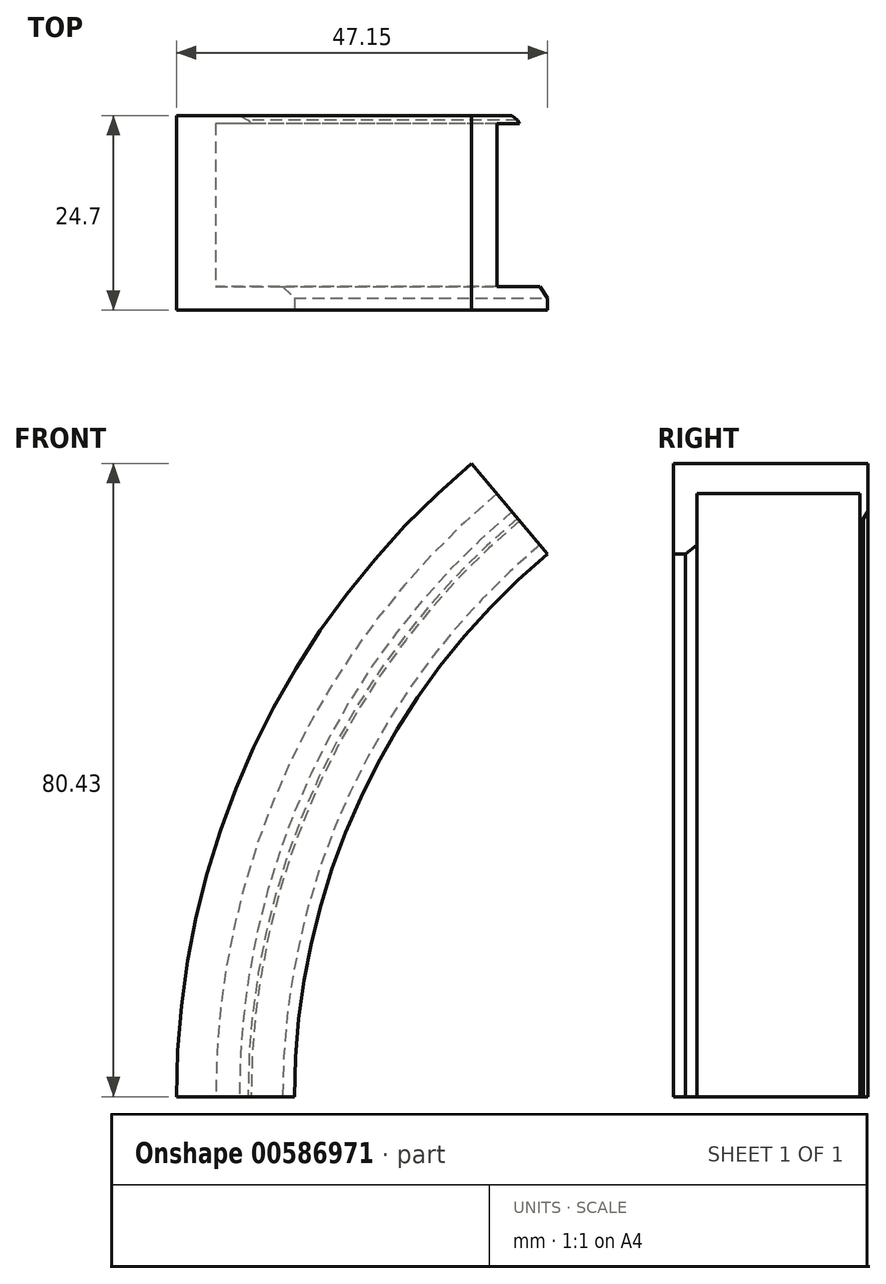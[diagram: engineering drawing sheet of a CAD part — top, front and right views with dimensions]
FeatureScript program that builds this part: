
annotation { "Feature Type Name" : "Feature", "Feature Type Description" : "" }
export const myFeature = defineFeature(function(context is Context, id is Id, definition is map)
    precondition{}
    {
        {
            var Q0;
            Q0=qCreatedBy(makeId("Top.planeOp"),FACE);
            var sketch = newSketch(context, id + "F0", { "sketchPlane" : qUnion([Q0])});
            skLineSegment(sketch, "E0", {"start": v(-100, -10) * mm, "end": v(-90, -10) * mm});
            skLineSegment(sketch, "E1", {"start": v(-90, -10) * mm, "end": v(-90, -13) * mm});
            skLineSegment(sketch, "E2", {"start": v(-90, -13) * mm, "end": v(-105, -13) * mm});
            skLineSegment(sketch, "E3", {"start": v(-105, -13) * mm, "end": v(-105, 11.7) * mm});
            skLineSegment(sketch, "E4", {"start": v(-105, 11.7) * mm, "end": v(-97, 11.7) * mm});
            skLineSegment(sketch, "E5", {"start": v(-97, 11.7) * mm, "end": v(-95, 10.7) * mm});
            skLineSegment(sketch, "E6", {"start": v(-95, 10.7) * mm, "end": v(-100, 10.7) * mm});
            skLineSegment(sketch, "E7", {"start": v(-100, 10.7) * mm, "end": v(-100, -10) * mm});
            skLineSegment(sketch, "E8", {"start": v(0, 38.45) * mm, "end": v(0, -30.66) * mm});
            skSolve(sketch);
        }
        {
            var Q0;
            Q0 = qSketchRegion(id + "F0", true);
            var Q1;
            Q1=sQuery(id+"F0.wireOp",EDGE,"E8");
            revolve(context, id + "F1", {"entities" : qUnion([Q0]), "axis" : qUnion([Q1]), "revolveType" : RevolveType.ONE_DIRECTION, "oppositeDirection" : true, "angle" : 50 * degree});
        }
        {
            var Q0;
            Q0=makeQuery(id+"F1.opRevolve","SWEPT_EDGE",EDGE,{"disambiguationData":[OSD([sQuery(id+"F0.wireOp",EDGE,"E0"),sQuery(id+"F0.wireOp",EDGE,"E1")])]});
            chamfer(context, id + "F2", {"entities" : qUnion([Q0]), "width" : 1.5 * mm, "tangentPropagation" : true});
        }
        {
            var Q0;
            Q0=makeQuery(id+"F1.opRevolve","SWEPT_EDGE",EDGE,{"disambiguationData":[OSD([sQuery(id+"F0.wireOp",EDGE,"E5"),sQuery(id+"F0.wireOp",EDGE,"E6")])]});
            chamfer(context, id + "F3", {"entities" : qUnion([Q0]), "chamferType" : ChamferType.TWO_OFFSETS, "width1" : 1 * mm, "oppositeDirection" : false, "width2" : .5 * mm, "tangentPropagation" : true});
        }
    });
